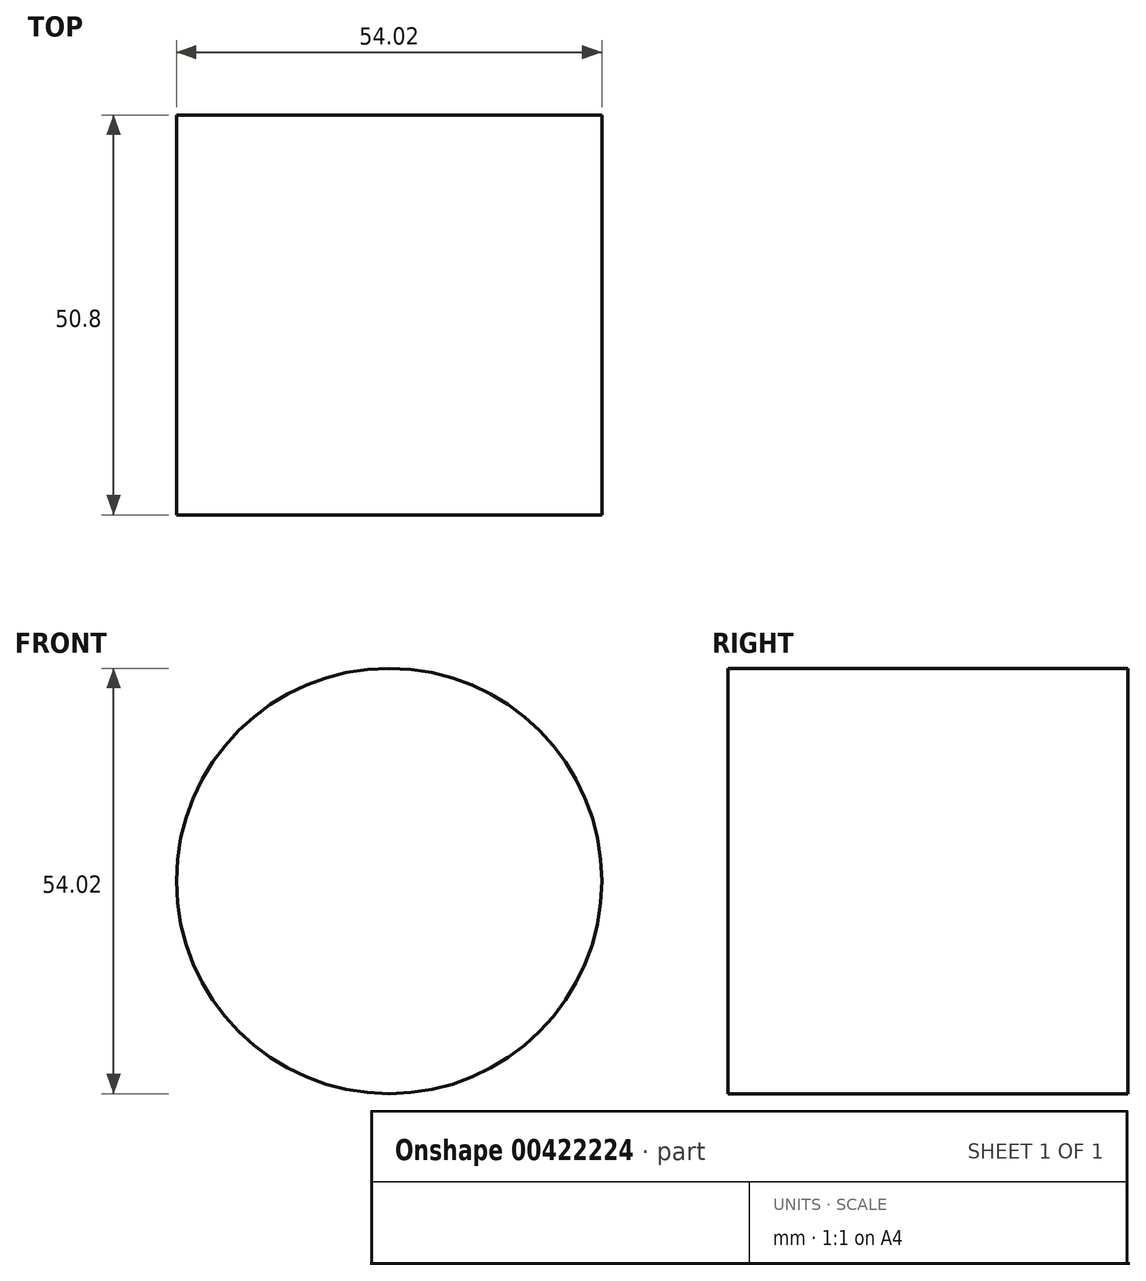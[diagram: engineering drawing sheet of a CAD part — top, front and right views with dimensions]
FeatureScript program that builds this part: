
annotation { "Feature Type Name" : "Feature", "Feature Type Description" : "" }
export const myFeature = defineFeature(function(context is Context, id is Id, definition is map)
    precondition{}
    {
        {
            var Q0;
            Q0=qCreatedBy(makeId("Front.planeOp"),FACE);
            var sketch = newSketch(context, id + "F0", { "sketchPlane" : qUnion([Q0])});
            skCircle(sketch, "E0", {"center": v(0, 0) * mm, "radius": 27.01 * mm});
            skSolve(sketch);
        }
        {
            var Q0;
            Q0=makeQuery(id+"F0.imprint","IMPRINT",FACE,{"disambiguationData":[TD([[makeQuery(id+"F0.imprint","IMPRINT",EDGE,{"derivedFrom":sQuery(id+"F0.wireOp",EDGE,"E0")}),1.0]])]});
            var sketch = newSketch(context, id + "F1", { "sketchPlane" : qUnion([Q0])});
            skSolve(sketch);
        }
        {
            var Q0;
            Q0=makeQuery(id+"F0.imprint","IMPRINT",FACE,{"disambiguationData":[TD([[makeQuery(id+"F0.imprint","IMPRINT",EDGE,{"derivedFrom":sQuery(id+"F0.wireOp",EDGE,"E0")}),1.0]])]});
            var Q1;
            Q1=makeQuery(id+"F1.imprint","IMPRINT",FACE,{"disambiguationData":[TD([[makeQuery(id+"F1.imprint","IMPRINT",EDGE,{"derivedFrom":makeQuery(id+"F0.imprint","IMPRINT",EDGE,{"derivedFrom":sQuery(id+"F0.wireOp",EDGE,"E0")})}),1.0]])]});
            extrude(context, id + "F2", {"entities" : qUnion([Q0, Q1]), "depth" : 50.8 * mm});
        }
    });
